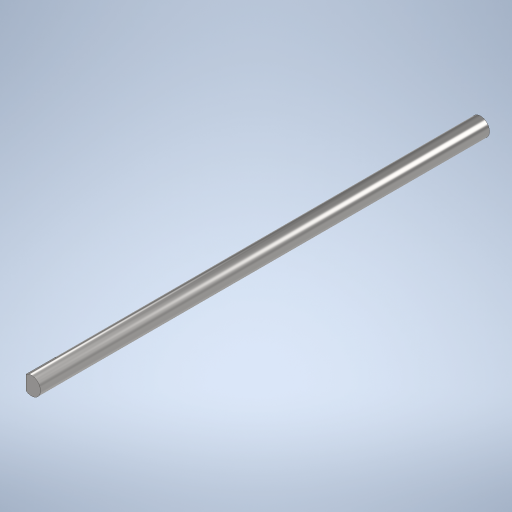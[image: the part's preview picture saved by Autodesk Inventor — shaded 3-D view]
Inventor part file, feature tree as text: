
AUTODESK INVENTOR PART (.ipt)
format: ipt  version: 2023.2 (Build 272271000, 271)  size: 272,896 bytes
history: native  units: mm
features: extrude x2, sketch x2
ambient origin geometry x8: Origin, YZ Plane, XZ Plane, XY Plane, X Axis, Y Axis, Z Axis, Center Point
bodies: Solid1 (feature_tree)
feature tree (4):
  extrude  "Extrusion1"  Depth=300.0mm TaperAngle=0.0deg
  extrude  "Extrusion4"  Depth=20.0mm
  sketch  "Sketch1"  dims[d0=12.0mm d1=300.0mm d2=0.0mm]
  sketch  "Sketch4"  dims[d7=20.0mm d8=0.0mm d5=0.5mm d6=0.872665mm]
